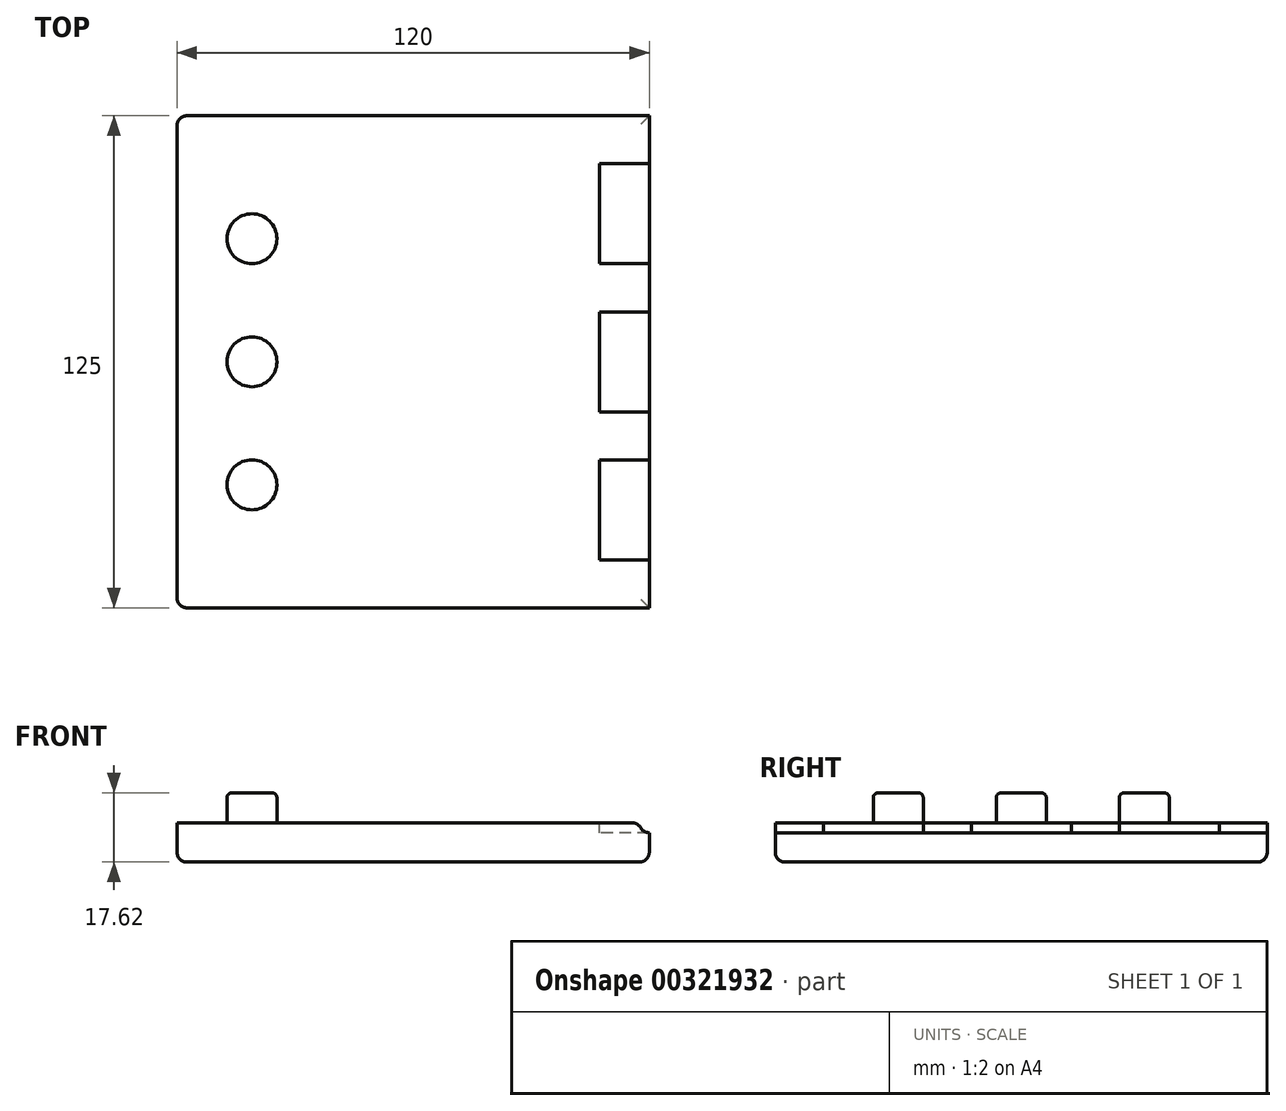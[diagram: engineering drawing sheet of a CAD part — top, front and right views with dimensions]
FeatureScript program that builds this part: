
annotation { "Feature Type Name" : "Feature", "Feature Type Description" : "" }
export const myFeature = defineFeature(function(context is Context, id is Id, definition is map)
    precondition{}
    {
        {
            var Q0;
            Q0=qCreatedBy(makeId("Top.planeOp"),FACE);
            var sketch = newSketch(context, id + "F0", { "sketchPlane" : qUnion([Q0])});
            skLineSegment(sketch, "E0.bottom", {"start": v(-60, -62.5) * mm, "end": v(60, -62.5) * mm});
            skLineSegment(sketch, "E0.top", {"start": v(-60, 62.5) * mm, "end": v(60, 62.5) * mm});
            skLineSegment(sketch, "E0.left", {"start": v(-60, -62.5) * mm, "end": v(-60, 62.5) * mm});
            skLineSegment(sketch, "E0.right", {"start": v(60, -62.5) * mm, "end": v(60, 62.5) * mm});
            skPoint(sketch, "E0.middle", {"position": v(0, 0) * mm});
            skSolve(sketch);
        }
        {
            var Q0;
            Q0 = qSketchRegion(id + "F0", true);
            extrude(context, id + "F1", {"entities" : qUnion([Q0]), "depth" : 10 * mm});
        }
        {
            var Q0;
            Q0=makeQuery(id+"F1.opExtrude","CAP_FACE",FACE,{"disambiguationData":[OSD([sQuery(id+"F0.wireOp",EDGE,"E0.bottom"),sQuery(id+"F0.wireOp",EDGE,"E0.top"),sQuery(id+"F0.wireOp",EDGE,"E0.left"),sQuery(id+"F0.wireOp",EDGE,"E0.right")])],"isStart":false});
            var sketch = newSketch(context, id + "F2", { "sketchPlane" : qUnion([Q0])});
            skLineSegment(sketch, "E1.bottom", {"start": v(60, -50.3) * mm, "end": v(47.3, -50.3) * mm});
            skLineSegment(sketch, "E1.top", {"start": v(60, -24.9) * mm, "end": v(47.3, -24.9) * mm});
            skLineSegment(sketch, "E1.left", {"start": v(60, -50.3) * mm, "end": v(60, -24.9) * mm});
            skLineSegment(sketch, "E1.right", {"start": v(47.3, -50.3) * mm, "end": v(47.3, -24.9) * mm});
            skLineSegment(sketch, "E2.bottom", {"start": v(60, -12.7) * mm, "end": v(47.3, -12.7) * mm});
            skLineSegment(sketch, "E2.right", {"start": v(47.3, -12.7) * mm, "end": v(47.3, 0) * mm});
            skLineSegment(sketch, "E3", {"start": v(47.3, 0) * mm, "end": v(47.3, -62.5) * mm, "construction": true});
            skLineSegment(sketch, "E4", {"start": v(3.01, 0) * mm, "end": v(47.3, 0) * mm, "construction": true});
            skLineSegment(sketch, "E5.MirrorCS", {"start": v(47.3, 0) * mm, "end": v(47.3, 62.5) * mm, "construction": true});
            skLineSegment(sketch, "E6.MirrorCS", {"start": v(60, 12.7) * mm, "end": v(47.3, 12.7) * mm});
            skLineSegment(sketch, "E7.MirrorCS", {"start": v(60, 24.9) * mm, "end": v(47.3, 24.9) * mm});
            skLineSegment(sketch, "E8.MirrorCS", {"start": v(60, 50.3) * mm, "end": v(47.3, 50.3) * mm});
            skLineSegment(sketch, "E9.MirrorCS", {"start": v(60, 50.3) * mm, "end": v(60, 24.9) * mm});
            skLineSegment(sketch, "E10", {"start": v(47.3, 0) * mm, "end": v(47.3, 12.7) * mm});
            skLineSegment(sketch, "E11", {"start": v(47.3, 24.9) * mm, "end": v(47.3, 50.3) * mm});
            skLineSegment(sketch, "E12", {"start": v(60, -12.7) * mm, "end": v(60, 12.7) * mm});
            skSolve(sketch);
        }
        {
            var Q0;
            Q0 = qSketchRegion(id + "F2", true);
            extrude(context, id + "F3", {"entities" : qUnion([Q0]), "operationType" : NewBodyOperationType.REMOVE, "oppositeDirection" : true, "depth" : 2.54 * mm});
        }
        {
            var Q0;
            Q0=makeQuery(id+"F1.opExtrude","CAP_FACE",FACE,{"disambiguationData":[OSD([sQuery(id+"F0.wireOp",EDGE,"E0.bottom"),sQuery(id+"F0.wireOp",EDGE,"E0.top"),sQuery(id+"F0.wireOp",EDGE,"E0.left"),sQuery(id+"F0.wireOp",EDGE,"E0.right")])],"isStart":false});
            var sketch = newSketch(context, id + "F4", { "sketchPlane" : qUnion([Q0])});
            skLineSegment(sketch, "E13", {"start": v(0, 0) * mm, "end": v(-60, 0) * mm, "construction": true});
            skCircle(sketch, "E14", {"center": v(-40.95, 0) * mm, "radius": 6.35 * mm});
            skLineSegment(sketch, "E15", {"start": v(-40.95, 0) * mm, "end": v(-40.95, -62.5) * mm, "construction": true});
            skCircle(sketch, "E16", {"center": v(-40.95, -31.25) * mm, "radius": 6.35 * mm});
            skCircle(sketch, "E17.MirrorC", {"center": v(-40.95, 31.25) * mm, "radius": 6.35 * mm});
            skSolve(sketch);
        }
        {
            var Q0;
            Q0 = qSketchRegion(id + "F4", true);
            extrude(context, id + "F5", {"entities" : qUnion([Q0]), "operationType" : NewBodyOperationType.ADD, "depth" : 7.62 * mm});
        }
        {
            var Q0;
            Q0=makeQuery(id+"F5.opExtrude","CAP_EDGE",EDGE,{"disambiguationData":[OSD([sQuery(id+"F4.wireOp",EDGE,"E16")])],"isStart":false});
            var Q1;
            Q1=makeQuery(id+"F5.opExtrude","CAP_EDGE",EDGE,{"disambiguationData":[OSD([sQuery(id+"F4.wireOp",EDGE,"E14")])],"isStart":false});
            var Q2;
            Q2=makeQuery(id+"F5.opExtrude","CAP_EDGE",EDGE,{"disambiguationData":[OSD([sQuery(id+"F4.wireOp",EDGE,"E17.MirrorC")])],"isStart":false});
            fillet(context, id + "F6", {"entities" : qUnion([Q0, Q1, Q2]), "radius" : 1.27 * mm, "tangentPropagation" : true, "allowEdgeOverflow" : false});
        }
        {
            var Q0;
            Q0=makeQuery(id+"F1.opExtrude","SWEPT_EDGE",EDGE,{"disambiguationData":[OSD([sQuery(id+"F0.wireOp",EDGE,"E0.top"),sQuery(id+"F0.wireOp",EDGE,"E0.left")])]});
            var Q1;
            Q1=makeQuery(id+"F1.opExtrude","SWEPT_EDGE",EDGE,{"disambiguationData":[OSD([sQuery(id+"F0.wireOp",EDGE,"E0.bottom"),sQuery(id+"F0.wireOp",EDGE,"E0.left")])]});
            var Q2;
            Q2=makeQuery(id+"F1.opExtrude","CAP_EDGE",EDGE,{"disambiguationData":[OSD([sQuery(id+"F0.wireOp",EDGE,"E0.top")])],"isStart":true});
            var Q3;
            Q3=makeQuery(id+"F1.opExtrude","CAP_EDGE",EDGE,{"disambiguationData":[OSD([sQuery(id+"F0.wireOp",EDGE,"E0.left")])],"isStart":true});
            var Q4;
            Q4=makeQuery(id+"F1.opExtrude","CAP_EDGE",EDGE,{"disambiguationData":[OSD([sQuery(id+"F0.wireOp",EDGE,"E0.bottom")])],"isStart":true});
            var Q5;
            Q5=makeQuery(id+"F1.opExtrude","CAP_EDGE",EDGE,{"disambiguationData":[OSD([sQuery(id+"F0.wireOp",EDGE,"E0.right")])],"isStart":true});
            fillet(context, id + "F7", {"entities" : qUnion([Q0, Q1, Q2, Q3, Q4, Q5]), "radius" : 2.54 * mm, "tangentPropagation" : true, "allowEdgeOverflow" : false});
        }
        {
            var Q0;
            Q0=makeQuery(id+"F1.opExtrude","SWEPT_FACE",FACE,{"disambiguationData":[OSD([sQuery(id+"F0.wireOp",EDGE,"E0.bottom")])]});
            var sketch = newSketch(context, id + "F8", { "sketchPlane" : qUnion([Q0])});
            skCircle(sketch, "E18", {"center": v(60, 10) * mm, "radius": 2.54 * mm});
            skSolve(sketch);
        }
        {
            var Q0;
            Q0 = qSketchRegion(id + "F8", true);
            extrude(context, id + "F9", {"entities" : qUnion([Q0]), "operationType" : NewBodyOperationType.REMOVE, "endBound" : BoundingType.THROUGH_ALL, "oppositeDirection" : true, "depth" : 25.4 * mm});
        }
        {
            var Q0;
            Q0=makeQuery(id+"F9.boolean.opBoolean","INTERSECT",EDGE,{"disambiguationData":[OD(0.0)],"derivedFrom":[makeQuery(id+"F1.opExtrude","CAP_FACE",FACE,{"disambiguationData":[OSD([sQuery(id+"F0.wireOp",EDGE,"E0.bottom"),sQuery(id+"F0.wireOp",EDGE,"E0.top"),sQuery(id+"F0.wireOp",EDGE,"E0.left"),sQuery(id+"F0.wireOp",EDGE,"E0.right")])],"isStart":false}),makeQuery(id+"F9.opExtrude","SWEPT_FACE",FACE,{"disambiguationData":[OSD([sQuery(id+"F8.wireOp",EDGE,"E18")])]})]});
            var Q1;
            Q1=makeQuery(id+"F9.boolean.opBoolean","INTERSECT",EDGE,{"disambiguationData":[OD(1.0)],"derivedFrom":[makeQuery(id+"F1.opExtrude","CAP_FACE",FACE,{"disambiguationData":[OSD([sQuery(id+"F0.wireOp",EDGE,"E0.bottom"),sQuery(id+"F0.wireOp",EDGE,"E0.top"),sQuery(id+"F0.wireOp",EDGE,"E0.left"),sQuery(id+"F0.wireOp",EDGE,"E0.right")])],"isStart":false}),makeQuery(id+"F9.opExtrude","SWEPT_FACE",FACE,{"disambiguationData":[OSD([sQuery(id+"F8.wireOp",EDGE,"E18")])]})]});
            var Q2;
            Q2=makeQuery(id+"F9.boolean.opBoolean","INTERSECT",EDGE,{"disambiguationData":[OD(2.0)],"derivedFrom":[makeQuery(id+"F1.opExtrude","CAP_FACE",FACE,{"disambiguationData":[OSD([sQuery(id+"F0.wireOp",EDGE,"E0.bottom"),sQuery(id+"F0.wireOp",EDGE,"E0.top"),sQuery(id+"F0.wireOp",EDGE,"E0.left"),sQuery(id+"F0.wireOp",EDGE,"E0.right")])],"isStart":false}),makeQuery(id+"F9.opExtrude","SWEPT_FACE",FACE,{"disambiguationData":[OSD([sQuery(id+"F8.wireOp",EDGE,"E18")])]})]});
            var Q3;
            Q3=makeQuery(id+"F9.boolean.opBoolean","INTERSECT",EDGE,{"disambiguationData":[OD(3.0)],"derivedFrom":[makeQuery(id+"F1.opExtrude","CAP_FACE",FACE,{"disambiguationData":[OSD([sQuery(id+"F0.wireOp",EDGE,"E0.bottom"),sQuery(id+"F0.wireOp",EDGE,"E0.top"),sQuery(id+"F0.wireOp",EDGE,"E0.left"),sQuery(id+"F0.wireOp",EDGE,"E0.right")])],"isStart":false}),makeQuery(id+"F9.opExtrude","SWEPT_FACE",FACE,{"disambiguationData":[OSD([sQuery(id+"F8.wireOp",EDGE,"E18")])]})]});
            fillet(context, id + "F10", {"entities" : qUnion([Q0, Q1, Q2, Q3]), "radius" : 2.54 * mm, "tangentPropagation" : true, "allowEdgeOverflow" : false});
        }
    });
